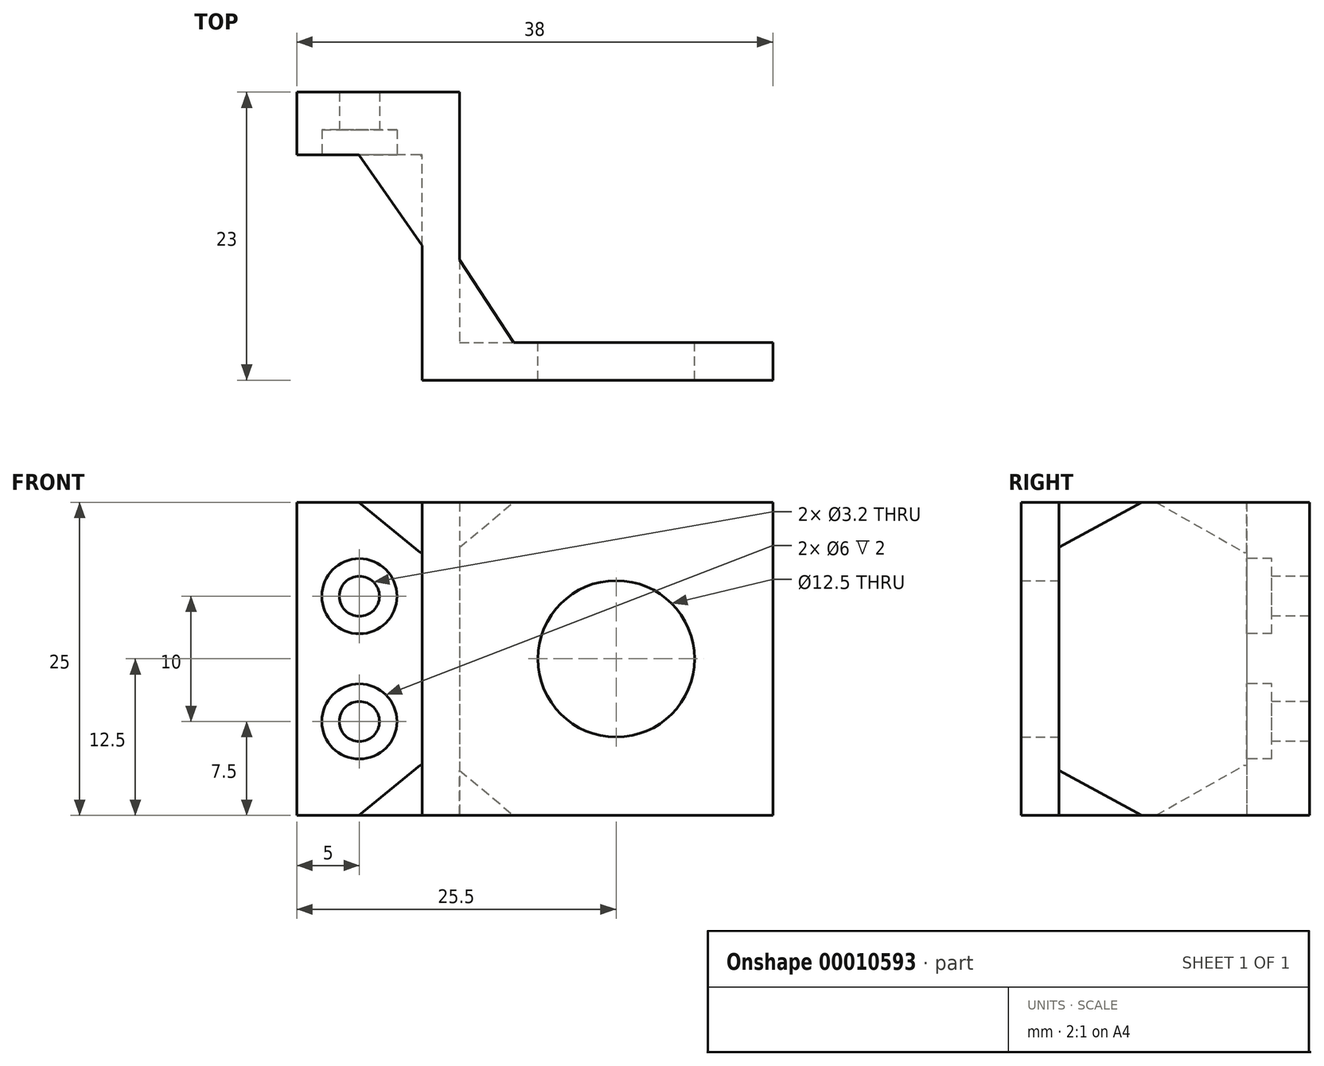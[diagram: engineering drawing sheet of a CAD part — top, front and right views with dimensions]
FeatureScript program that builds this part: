
annotation { "Feature Type Name" : "Feature", "Feature Type Description" : "" }
export const myFeature = defineFeature(function(context is Context, id is Id, definition is map)
    precondition{}
    {
        {
            var Q0;
            Q0=qCreatedBy(makeId("Top.planeOp"),FACE);
            var sketch = newSketch(context, id + "F0", { "sketchPlane" : qUnion([Q0])});
            skLineSegment(sketch, "E0", {"start": v(0, 0) * mm, "end": v(25, 0) * mm});
            skLineSegment(sketch, "E1", {"start": v(25, 0) * mm, "end": v(25, -3) * mm});
            skLineSegment(sketch, "E2", {"start": v(25, -3) * mm, "end": v(-3, -3) * mm});
            skLineSegment(sketch, "E3", {"start": v(-3, -3) * mm, "end": v(-3, 15) * mm});
            skLineSegment(sketch, "E4", {"start": v(-3, 15) * mm, "end": v(-13, 15) * mm});
            skLineSegment(sketch, "E5", {"start": v(-13, 15) * mm, "end": v(-13, 20) * mm});
            skLineSegment(sketch, "E6", {"start": v(-13, 20) * mm, "end": v(0, 20) * mm});
            skLineSegment(sketch, "E7", {"start": v(0, 20) * mm, "end": v(0, 0) * mm});
            skSolve(sketch);
        }
        {
            var Q0;
            Q0 = qSketchRegion(id + "F0", true);
            extrude(context, id + "F1", {"entities" : qUnion([Q0]), "depth" : 25 * mm});
        }
        {
            var Q0;
            Q0=makeQuery(id+"F1.opExtrude","SWEPT_FACE",FACE,{"disambiguationData":[OSD([sQuery(id+"F0.wireOp",EDGE,"E0")])]});
            var sketch = newSketch(context, id + "F2", { "sketchPlane" : qUnion([Q0])});
            skLineSegment(sketch, "E8", {"start": v(-12.5, 0) * mm, "end": v(-12.5, 25) * mm, "construction": true});
            skCircle(sketch, "E9", {"center": v(-12.5, 12.5) * mm, "radius": 6.25 * mm});
            skSolve(sketch);
        }
        {
            var Q0;
            Q0 = qSketchRegion(id + "F2", true);
            extrude(context, id + "F3", {"entities" : qUnion([Q0]), "operationType" : NewBodyOperationType.REMOVE, "endBound" : BoundingType.UP_TO_NEXT, "oppositeDirection" : true, "depth" : 25 * mm});
        }
        {
            var Q0;
            Q0=makeQuery(id+"F1.opExtrude","SWEPT_FACE",FACE,{"disambiguationData":[OSD([sQuery(id+"F0.wireOp",EDGE,"E4")])]});
            var sketch = newSketch(context, id + "F4", { "sketchPlane" : qUnion([Q0])});
            skLineSegment(sketch, "E10", {"start": v(-13, 12.5) * mm, "end": v(-3, 12.5) * mm, "construction": true});
            skLineSegment(sketch, "E11", {"start": v(-8, 12.5) * mm, "end": v(-8, 7.5) * mm, "construction": true});
            skCircle(sketch, "E12", {"center": v(-8, 7.5) * mm, "radius": 1.6 * mm});
            skCircle(sketch, "E13.0.MirrorC", {"center": v(-8, 17.5) * mm, "radius": 1.6 * mm});
            skSolve(sketch);
        }
        {
            var Q0;
            Q0 = qSketchRegion(id + "F4", true);
            extrude(context, id + "F5", {"entities" : qUnion([Q0]), "operationType" : NewBodyOperationType.REMOVE, "endBound" : BoundingType.UP_TO_NEXT, "oppositeDirection" : true, "depth" : 25 * mm});
        }
        {
            var Q0;
            Q0=makeQuery(id+"F1.opExtrude","SWEPT_FACE",FACE,{"disambiguationData":[OSD([sQuery(id+"F0.wireOp",EDGE,"E4")])]});
            var sketch = newSketch(context, id + "F6", { "sketchPlane" : qUnion([Q0])});
            skCircle(sketch, "E14", {"center": v(-8, 7.5) * mm, "radius": 3 * mm});
            skCircle(sketch, "E15", {"center": v(-8, 17.5) * mm, "radius": 3 * mm});
            skSolve(sketch);
        }
        {
            var Q0;
            Q0 = qSketchRegion(id + "F6", true);
            extrude(context, id + "F7", {"entities" : qUnion([Q0]), "operationType" : NewBodyOperationType.REMOVE, "oppositeDirection" : true, "depth" : 2 * mm});
        }
        {
            var Q0;
            Q0=makeQuery(id+"F1.opExtrude","CAP_FACE",FACE,{"disambiguationData":[OSD([sQuery(id+"F0.wireOp",EDGE,"E0"),sQuery(id+"F0.wireOp",EDGE,"E1"),sQuery(id+"F0.wireOp",EDGE,"E2"),sQuery(id+"F0.wireOp",EDGE,"E3"),sQuery(id+"F0.wireOp",EDGE,"E4"),sQuery(id+"F0.wireOp",EDGE,"E5"),sQuery(id+"F0.wireOp",EDGE,"E6"),sQuery(id+"F0.wireOp",EDGE,"E7")])],"isStart":true});
            var sketch = newSketch(context, id + "F8", { "sketchPlane" : qUnion([Q0])});
            skLineSegment(sketch, "E16", {"start": v(5.5, 0) * mm, "end": v(0, -8.44) * mm});
            skLineSegment(sketch, "E17", {"start": v(0, -8.44) * mm, "end": v(0, 0) * mm});
            skLineSegment(sketch, "E18", {"start": v(0, 0) * mm, "end": v(5.5, 0) * mm});
            skLineSegment(sketch, "E19", {"start": v(-9.24, -15) * mm, "end": v(-3, -6) * mm});
            skLineSegment(sketch, "E20", {"start": v(-3, -6) * mm, "end": v(-3, -15) * mm});
            skLineSegment(sketch, "E21", {"start": v(-3, -15) * mm, "end": v(-9.24, -15) * mm});
            skSolve(sketch);
        }
        {
            var Q0;
            Q0 = qSketchRegion(id + "F8", true);
            extrude(context, id + "F9", {"entities" : qUnion([Q0]), "operationType" : NewBodyOperationType.ADD, "oppositeDirection" : true, "depth" : 4 * mm});
        }
        {
            var Q0;
            Q0=makeQuery(id+"F1.opExtrude","CAP_FACE",FACE,{"disambiguationData":[OSD([sQuery(id+"F0.wireOp",EDGE,"E0"),sQuery(id+"F0.wireOp",EDGE,"E1"),sQuery(id+"F0.wireOp",EDGE,"E2"),sQuery(id+"F0.wireOp",EDGE,"E3"),sQuery(id+"F0.wireOp",EDGE,"E4"),sQuery(id+"F0.wireOp",EDGE,"E5"),sQuery(id+"F0.wireOp",EDGE,"E6"),sQuery(id+"F0.wireOp",EDGE,"E7")])],"isStart":false});
            var sketch = newSketch(context, id + "F10", { "sketchPlane" : qUnion([Q0])});
            skLineSegment(sketch, "E22.0.0", {"start": v(5.5, 0) * mm, "end": v(0, 8.44) * mm});
            skLineSegment(sketch, "E22.0.1", {"start": v(0, 8.44) * mm, "end": v(0, 0) * mm});
            skLineSegment(sketch, "E22.0.2", {"start": v(0, 0) * mm, "end": v(5.5, 0) * mm});
            skLineSegment(sketch, "E23.0", {"start": v(-9.24, 15) * mm, "end": v(-3, 6) * mm});
            skLineSegment(sketch, "E24", {"start": v(-3, 6) * mm, "end": v(-3, 15) * mm});
            skLineSegment(sketch, "E25", {"start": v(-3, 15) * mm, "end": v(-9.24, 15) * mm});
            skSolve(sketch);
        }
        {
            var Q0;
            Q0 = qSketchRegion(id + "F10", true);
            extrude(context, id + "F11", {"entities" : qUnion([Q0]), "operationType" : NewBodyOperationType.ADD, "oppositeDirection" : true, "depth" : 4 * mm});
        }
        {
            var Q0;
            Q0=makeQuery(id+"F9.opExtrude","CAP_EDGE",EDGE,{"disambiguationData":[OSD([sQuery(id+"F8.wireOp",EDGE,"E19")])],"isStart":false});
            var Q1;
            Q1=makeQuery(id+"F11.opExtrude","CAP_EDGE",EDGE,{"disambiguationData":[OSD([sQuery(id+"F10.wireOp",EDGE,"E23.0")])],"isStart":false});
            var Q2;
            Q2=makeQuery(id+"F11.opExtrude","CAP_EDGE",EDGE,{"disambiguationData":[OSD([sQuery(id+"F10.wireOp",EDGE,"E22.0.0")])],"isStart":false});
            var Q3;
            Q3=makeQuery(id+"F9.opExtrude","CAP_EDGE",EDGE,{"disambiguationData":[OSD([sQuery(id+"F8.wireOp",EDGE,"E16")])],"isStart":false});
            chamfer(context, id + "F12", {"entities" : qUnion([Q0, Q1, Q2, Q3]), "chamferType" : ChamferType.OFFSET_ANGLE, "width" : 5 * mm, "oppositeDirection" : false, "angle" : 45 * degree, "tangentPropagation" : true});
        }
    });
